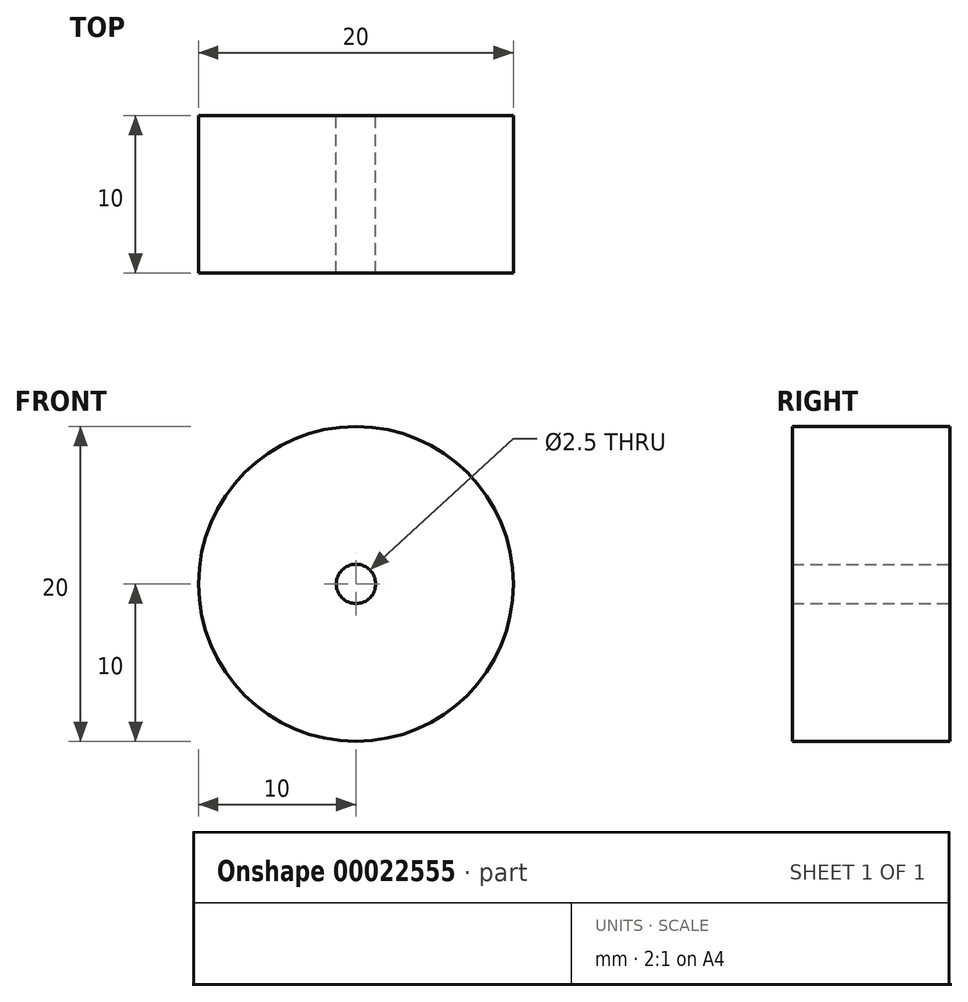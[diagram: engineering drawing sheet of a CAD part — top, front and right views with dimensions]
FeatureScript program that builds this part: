
annotation { "Feature Type Name" : "Feature", "Feature Type Description" : "" }
export const myFeature = defineFeature(function(context is Context, id is Id, definition is map)
    precondition{}
    {
        {
            var Q0;
            Q0=qCreatedBy(makeId("Front.planeOp"),FACE);
            var sketch = newSketch(context, id + "F0", { "sketchPlane" : qUnion([Q0])});
            skCircle(sketch, "E0", {"center": v(0, 0) * mm, "radius": 10 * mm});
            skCircle(sketch, "E1", {"center": v(0, 0) * mm, "radius": 1.25 * mm});
            skSolve(sketch);
        }
        {
            var Q0;
            Q0=makeQuery(id+"F0.imprint","IMPRINT",FACE,{"disambiguationData":[TD([[makeQuery(id+"F0.imprint","IMPRINT",EDGE,{"derivedFrom":sQuery(id+"F0.wireOp",EDGE,"E0")}),1.0]])]});
            extrude(context, id + "F1", {"entities" : qUnion([Q0]), "depth" : 10 * mm});
        }
    });
